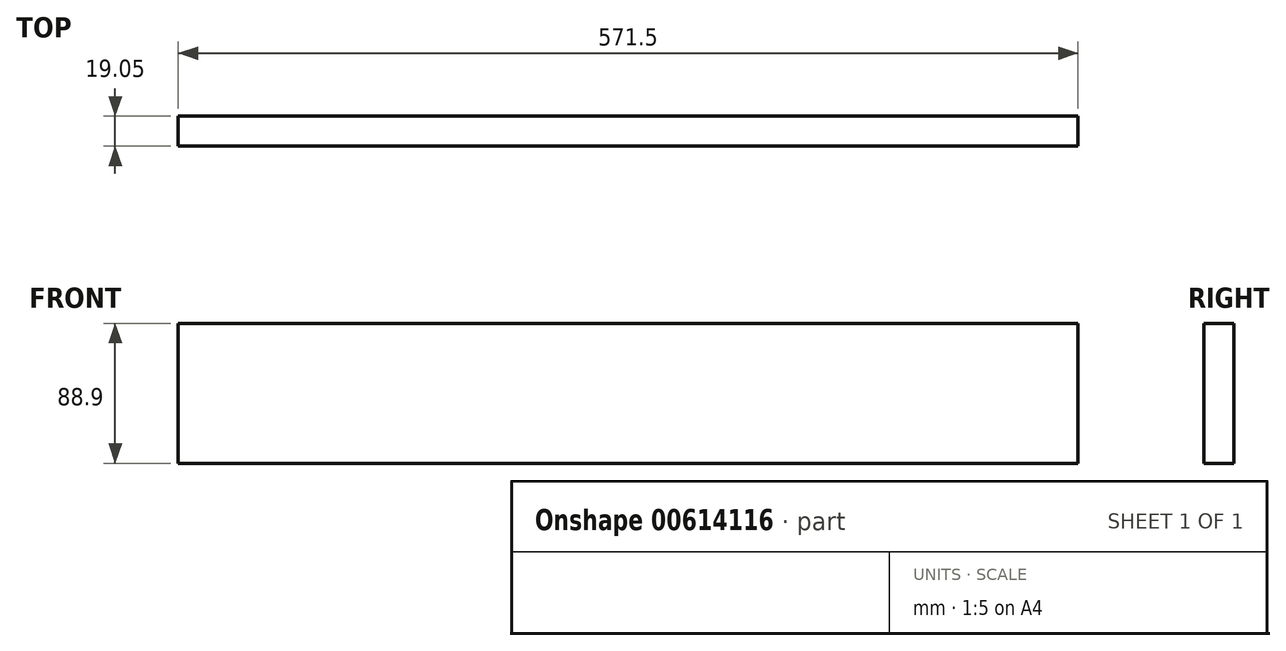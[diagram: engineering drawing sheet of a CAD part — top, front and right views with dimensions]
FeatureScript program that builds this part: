
annotation { "Feature Type Name" : "Feature", "Feature Type Description" : "" }
export const myFeature = defineFeature(function(context is Context, id is Id, definition is map)
    precondition{}
    {
        {
            var Q0;
            Q0=qCreatedBy(makeId("Front.planeOp"),FACE);
            var sketch = newSketch(context, id + "F0", { "sketchPlane" : qUnion([Q0])});
            skLineSegment(sketch, "E0.bottom", {"start": v(285.75, 44.45) * mm, "end": v(-285.75, 44.45) * mm});
            skLineSegment(sketch, "E0.top", {"start": v(285.75, -44.45) * mm, "end": v(-285.75, -44.45) * mm});
            skLineSegment(sketch, "E0.left", {"start": v(285.75, 44.45) * mm, "end": v(285.75, -44.45) * mm});
            skLineSegment(sketch, "E0.right", {"start": v(-285.75, 44.45) * mm, "end": v(-285.75, -44.45) * mm});
            skPoint(sketch, "E0.middle", {"position": v(0, 0) * mm});
            skSolve(sketch);
        }
        {
            var Q0;
            Q0=makeQuery(id+"F0.imprint","IMPRINT",FACE,{"disambiguationData":[TD([[makeQuery(id+"F0.imprint","IMPRINT",EDGE,{"derivedFrom":sQuery(id+"F0.wireOp",EDGE,"E0.bottom")}),1.0]])]});
            extrude(context, id + "F1", {"entities" : qUnion([Q0]), "depth" : 19.05 * mm, "offsetDistance" : 25.4 * mm});
        }
    });
